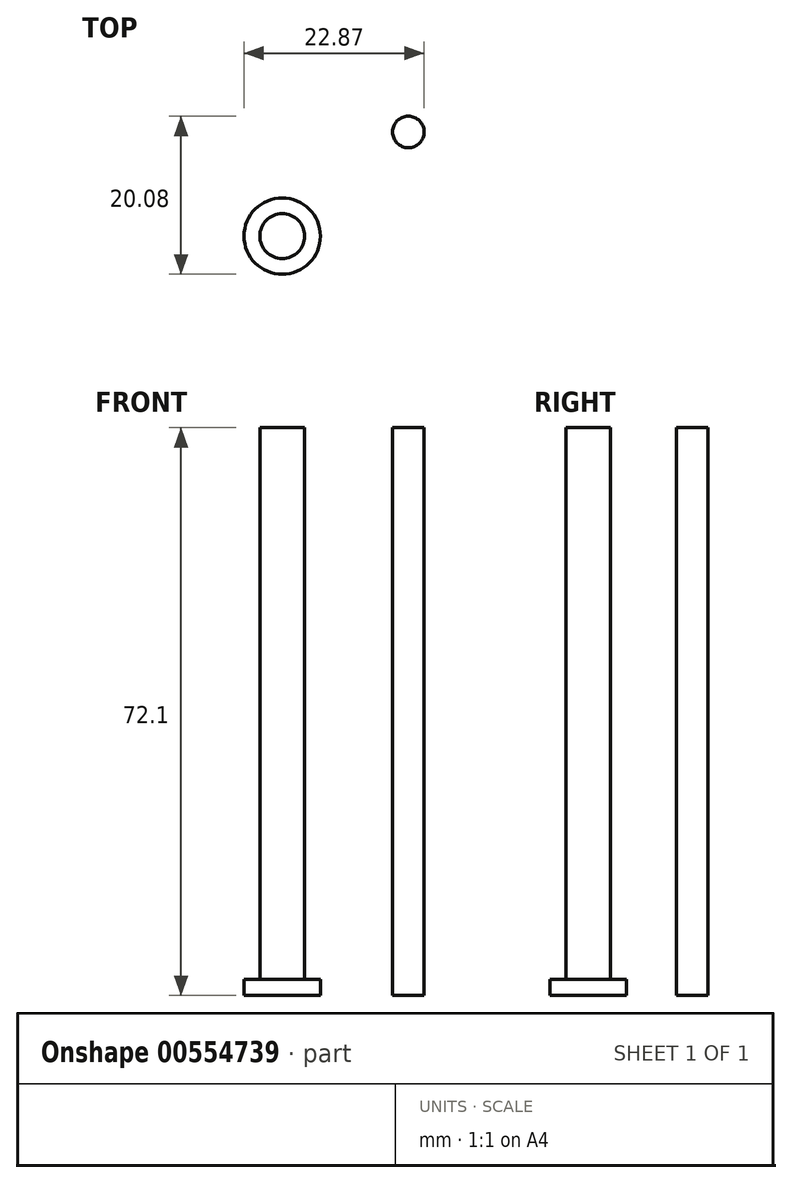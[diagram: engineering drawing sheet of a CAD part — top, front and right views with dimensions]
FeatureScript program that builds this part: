
annotation { "Feature Type Name" : "Feature", "Feature Type Description" : "" }
export const myFeature = defineFeature(function(context is Context, id is Id, definition is map)
    precondition{}
    {
        {
            var Q0;
            Q0=qCreatedBy(makeId("Top.planeOp"),FACE);
            var sketch = newSketch(context, id + "F0", { "sketchPlane" : qUnion([Q0])});
            skCircle(sketch, "E0", {"center": v(0, 0) * mm, "radius": 2.85 * mm});
            skCircle(sketch, "E1.0", {"center": v(0, 0) * mm, "radius": 4.85 * mm});
            skCircle(sketch, "E2", {"center": v(16.02, 13.23) * mm, "radius": 2 * mm});
            skSolve(sketch);
        }
        {
            var Q0;
            Q0=makeQuery(id+"F0.imprint","IMPRINT",FACE,{"disambiguationData":[TD([[makeQuery(id+"F0.imprint","IMPRINT",EDGE,{"derivedFrom":sQuery(id+"F0.wireOp",EDGE,"E0")}),1.0]])]});
            var Q1;
            Q1=makeQuery(id+"F0.imprint","IMPRINT",FACE,{"disambiguationData":[TD([[makeQuery(id+"F0.imprint","IMPRINT",EDGE,{"derivedFrom":sQuery(id+"F0.wireOp",EDGE,"E2")}),1.0]])]});
            extrude(context, id + "F1", {"entities" : qUnion([Q0, Q1]), "depth" : 70.1 * mm, "offsetDistance" : 25 * mm});
        }
        {
            var Q0;
            Q0=makeQuery(id+"F0.imprint","IMPRINT",FACE,{"disambiguationData":[TD([[makeQuery(id+"F0.imprint","IMPRINT",EDGE,{"derivedFrom":sQuery(id+"F0.wireOp",EDGE,"E0")}),-1.0]])]});
            var Q1;
            Q1=makeQuery(id+"F1.opExtrude","CAP_FACE",FACE,{"disambiguationData":[OSD([sQuery(id+"F0.wireOp",EDGE,"E0")])],"isStart":true});
            var Q2;
            Q2=makeQuery(id+"F0.imprint","IMPRINT",FACE,{"disambiguationData":[TD([[makeQuery(id+"F0.imprint","IMPRINT",EDGE,{"derivedFrom":sQuery(id+"F0.wireOp",EDGE,"E2")}),1.0]])]});
            extrude(context, id + "F2", {"entities" : qUnion([Q0, Q1, Q2]), "operationType" : NewBodyOperationType.ADD, "oppositeDirection" : true, "depth" : 2 * mm, "offsetDistance" : 25 * mm});
        }
    });
